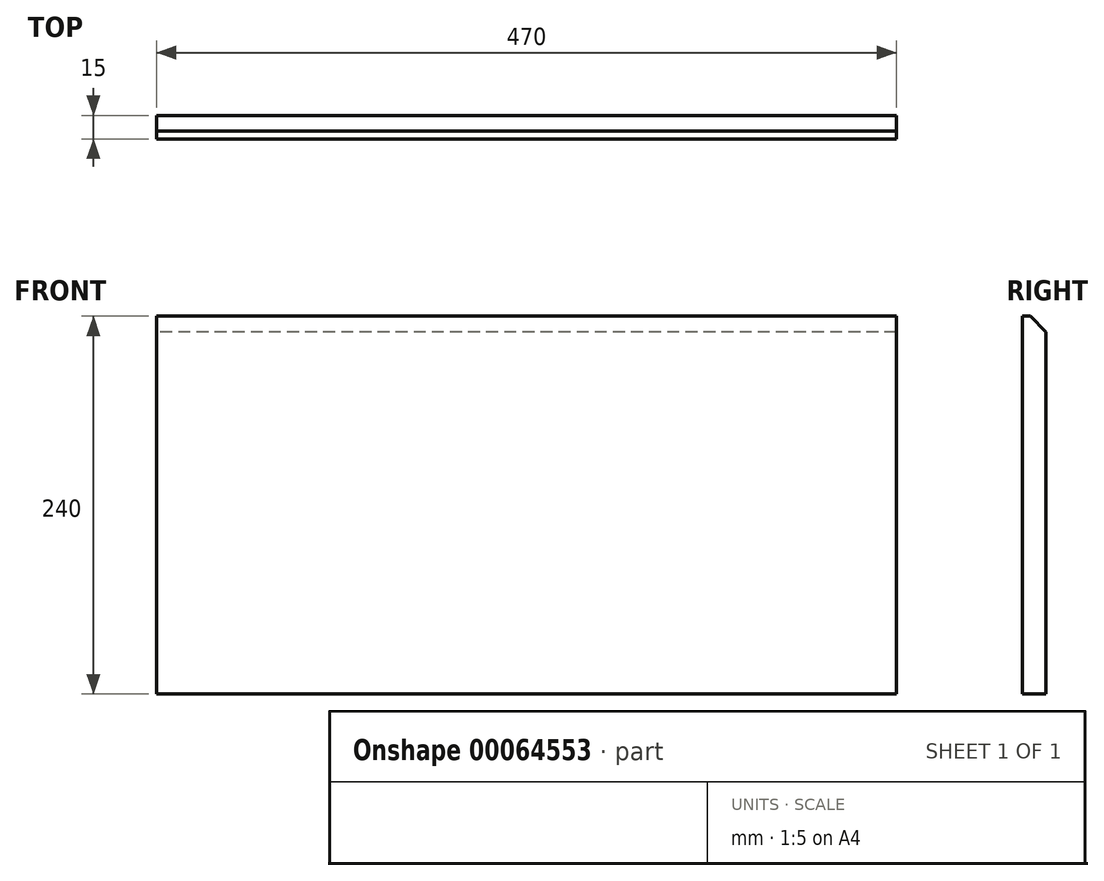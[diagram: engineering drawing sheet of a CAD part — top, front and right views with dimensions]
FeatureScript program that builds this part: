
annotation { "Feature Type Name" : "Feature", "Feature Type Description" : "" }
export const myFeature = defineFeature(function(context is Context, id is Id, definition is map)
    precondition{}
    {
        {
            var Q0;
            Q0=qCreatedBy(makeId("Right.planeOp"),FACE);
            var sketch = newSketch(context, id + "F0", { "sketchPlane" : qUnion([Q0])});
            skLineSegment(sketch, "E0", {"start": v(-42.97, -126.66) * mm, "end": v(-27.97, -126.66) * mm});
            skLineSegment(sketch, "E1", {"start": v(-27.97, -126.66) * mm, "end": v(-27.97, 103.34) * mm});
            skLineSegment(sketch, "E2", {"start": v(-27.97, 103.34) * mm, "end": v(-37.97, 113.34) * mm});
            skLineSegment(sketch, "E3", {"start": v(-42.97, -126.66) * mm, "end": v(-42.97, 113.34) * mm});
            skLineSegment(sketch, "E4", {"start": v(-42.97, 113.34) * mm, "end": v(-37.97, 113.34) * mm});
            skSolve(sketch);
        }
        {
            var Q0;
            Q0 = qSketchRegion(id + "F0", true);
            extrude(context, id + "F1", {"entities" : qUnion([Q0]), "depth" : 470 * mm});
        }
    });
